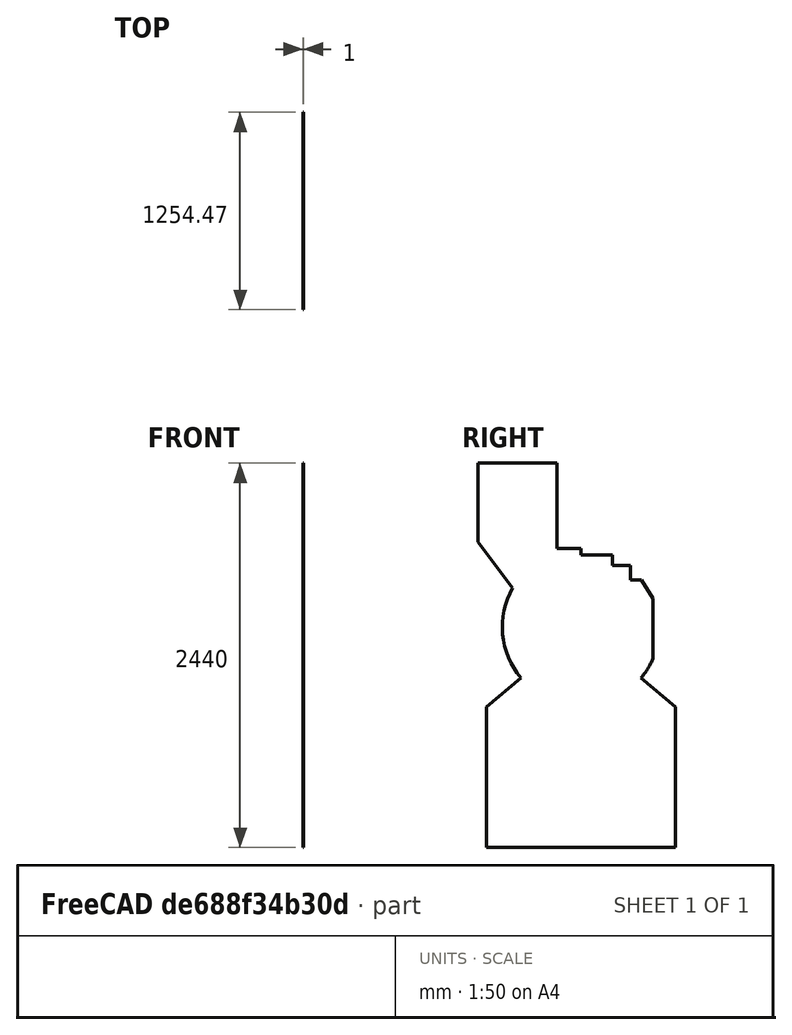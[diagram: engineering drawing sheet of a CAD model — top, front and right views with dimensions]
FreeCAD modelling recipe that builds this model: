
FCSTD DOCUMENT
Label: Shell Front
objects: Sketcher::SketchObject×1, PartDesign::Pad×1
note: 3 computed .brp shape members not serialized (recipe doc carries the construction recipe); baked Part::Feature solids carry a one-line shape summary decoded from their .brp

FEATURE [Sketcher::SketchObject] Sketch
  Placement = pos=(500,0,0) rot=(0.57735,0.57735,0.57735;2.0944rad)
  sketch-geometry (20):
    g0: ArcOfCircle CenterX=0 CenterY=0 CenterZ=0 NormalX=0 NormalY=0 NormalZ=1 Radius=500 StartAngle=2.6242 EndAngle=3.84621
    g1: LineSegment StartX=-434.557 StartY=247.306 StartZ=0 EndX=-654.474 EndY=540 EndZ=0
    g2: LineSegment StartX=-152.007 StartY=500 StartZ=0 EndX=-0.000113022 EndY=500 EndZ=0
    g3: LineSegment StartX=-0.000113022 StartY=500 StartZ=0 EndX=-0.000113022 EndY=458.471 EndZ=0
    g4: LineSegment StartX=-0.000113022 StartY=458.471 StartZ=0 EndX=199.509 EndY=458.471 EndZ=0
    g5: LineSegment StartX=199.509 StartY=458.471 StartZ=0 EndX=199.509 EndY=390 EndZ=0
    g6: LineSegment StartX=199.509 StartY=390 StartZ=0 EndX=312.89 EndY=390 EndZ=0
    g7: LineSegment StartX=312.89 StartY=390 StartZ=0 EndX=312.89 EndY=297.137 EndZ=0
    g8: LineSegment StartX=312.89 StartY=297.137 StartZ=0 EndX=382.89 EndY=297.137 EndZ=0
    g9: LineSegment StartX=458.29 StartY=180.074 StartZ=0 EndX=458.29 EndY=-199.926 EndZ=0
    g10: LineSegment StartX=-654.474 StartY=1040 StartZ=0 EndX=-654.474 EndY=540 EndZ=0
    g11: LineSegment StartX=-380.931 StartY=-323.87 StartZ=0 EndX=-600 EndY=-507.691 EndZ=0
    g12: LineSegment StartX=-600 StartY=-507.691 StartZ=0 EndX=-600 EndY=-1400 EndZ=0
    g13: LineSegment StartX=-600 StartY=-1400 StartZ=0 EndX=600 EndY=-1400 EndZ=0
    g14: LineSegment StartX=600 StartY=-1400 StartZ=0 EndX=600 EndY=-507.691 EndZ=0
    g15: LineSegment StartX=600 StartY=-507.691 StartZ=0 EndX=380.931 EndY=-323.87 EndZ=0
    g16: LineSegment StartX=382.89 StartY=297.137 StartZ=0 EndX=458.29 EndY=180.074 EndZ=0
    g17: ArcOfCircle CenterX=0 CenterY=0 CenterZ=0 NormalX=0 NormalY=0 NormalZ=1 Radius=500 StartAngle=5.57857 EndAngle=5.87183
    g18: LineSegment StartX=-654.474 StartY=1040 StartZ=0 EndX=-152.007 EndY=1040 EndZ=0
    g19: LineSegment StartX=-152.007 StartY=1040 StartZ=0 EndX=-152.007 EndY=500 EndZ=0
  constraints (65):
    c: Radius(g0) = 500
    c: DistanceX(g0) = 0
    c: DistanceY(g0) = 0
    c: PointOnObject(g3,g0)
    c: Horizontal(g2)
    c: Vertical(g3)
    c: Coincident(g4,g3)
    c: PointOnObject(g5,g0)
    c: Horizontal(g4)
    c: Vertical(g5)
    c: Coincident(g6,g5)
    c: PointOnObject(g7,g0)
    c: Horizontal(g6)
    c: Vertical(g7)
    c: Coincident(g8,g7)
    c: Horizontal(g8)
    c: DistanceX(g1) = -654.474
    c: DistanceY(g1) = 540
    c: Coincident(g2,g3)
    c: Coincident(g4,g5)
    c: Coincident(g6,g7)
    c: Coincident(g9,g17)
    c: Vertical(g9)
    c: Distance(g9) = 380
    c: DistanceX(g2) = -152.007
    c: DistanceY(g2) = 500
    c: DistanceX(g5) = 199.509
    c: DistanceY(g5) = 390
    c: Distance(g8) = 70
    c: Coincident(g10,g1)
    c: Vertical(g10)
    c: Distance(g10) = 500
    c: Coincident(g12,g11)
    c: Vertical(g12)
    c: Horizontal(g13)
    c: Coincident(g14,g13)
    c: Vertical(g14)
    c: Coincident(g15,g14)
    c: Coincident(g13,g12)
    c: Equal(g14,g12)
    c: DistanceX(g13) = 600
    c: DistanceY(g13) = -1400
    c: Angle(g12,g11) = 2.26893
    c: Angle(g15,g14) = 2.26893
    c: Distance(g12) = 892.309
    c: Distance(g13) = 1200
    c: Coincident(g16,g8)
    c: Coincident(g16,g9)
    c: Distance(g16) = 139.244
    c: Distance(g7) = 92.8633
    c: Equal(g0,g17)
    c: Coincident(g0,g17)
    c: PointOnObject(g16,g17)
    c: PointOnObject(g16,g17)
    c: PointOnObject(g16,g17)
    c: PointOnObject(g16,g17)
    c: Coincident(g0,g11)
    c: Coincident(g15,g17)
    c: Coincident(g0,g1)
    c: Distance(g1) = 366.106
    c: Coincident(g18,g10)
    c: Horizontal(g18)
    c: Coincident(g19,g2)
    c: Vertical(g19)
    c: Coincident(g18,g19)
FEATURE [PartDesign::Pad] Pad
  Length = 1
  MirroredExtent = false
  Sketch = -> Sketch
